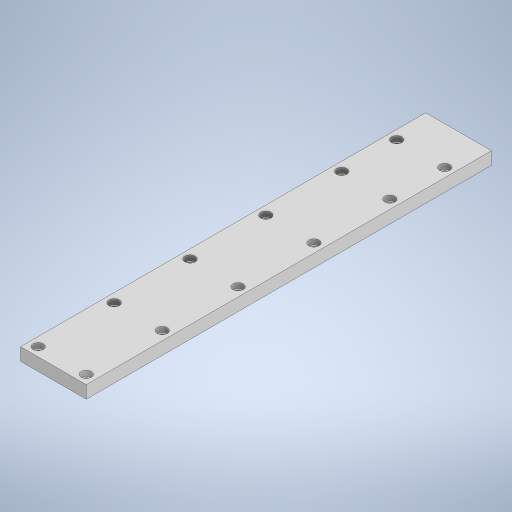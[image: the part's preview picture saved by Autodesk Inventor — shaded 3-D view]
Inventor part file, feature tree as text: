
AUTODESK INVENTOR PART (.ipt)
format: ipt  version: 2023 (Build 270158000, 158)  size: 359,936 bytes
history: native  units: mm
features: sketch x4, extrude x2, hole x2, fillet x1
ambient origin geometry x8: Origin, YZ Plane, XZ Plane, XY Plane, X Axis, Y Axis, Z Axis, Center Point
bodies: Solid1 (feature_tree)
feature tree (9):
  extrude  "Extrusion1"  Depth=26.0mm
  hole  "Hole1"  [1 undecoded]
  hole  "Hole2"  [1 undecoded]
  extrude  "Extrusion2"  Depth=0.5mm
  fillet  "Fillet2"  Radius=0.5mm
  sketch  "Sketch1"  dims[d0=160.2mm d1=26.0mm]
  sketch  "Sketch2"  dims[d2=5.0mm d3=0.0mm d4=3.5mm]
  sketch  "Sketch3"  dims[d5=3.5mm d6=50.0mm d8=30.0mm d9=10.0mm d11=10.0mm]
  sketch  "Sketch6"  dims[d13=15.0mm d14=2.38125mm d15=6.0mm d16=4.0mm d17=2.0mm d18=90.0deg d19=10.0mm d20=20.594885mm d22=3.0mm d23=2.38125mm d24=6.0mm d25=4.0mm d26=2.0mm d27=90.0deg d28=10.0mm d29=20.594885mm d36=0.5mm d37=0.0mm d38=1.5mm d40=0.5mm]
note: 2 required parameter values undecoded (feature->parameter linkage not recoverable at this tier; creation-order binding heuristic only, values carry confidence <= 0.55)
